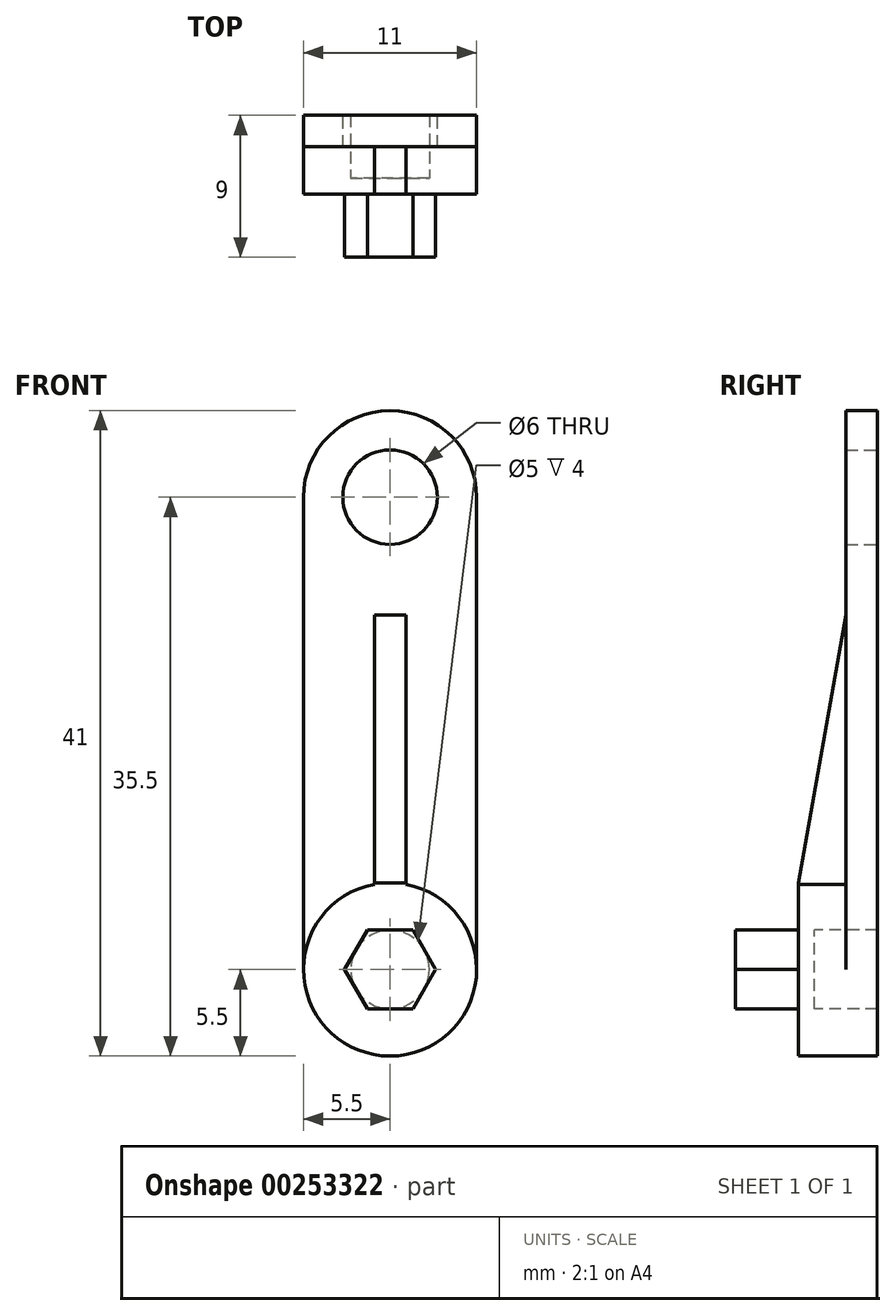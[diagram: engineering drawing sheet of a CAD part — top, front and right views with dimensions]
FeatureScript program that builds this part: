
annotation { "Feature Type Name" : "Feature", "Feature Type Description" : "" }
export const myFeature = defineFeature(function(context is Context, id is Id, definition is map)
    precondition{}
    {
        {
            var Q0;
            Q0=qCreatedBy(makeId("Front.planeOp"),FACE);
            var sketch = newSketch(context, id + "F0", { "sketchPlane" : qUnion([Q0])});
            skLineSegment(sketch, "E0", {"start": v(-5.5, 30) * mm, "end": v(-5.5, 0) * mm});
            skLineSegment(sketch, "E1", {"start": v(5.5, 30) * mm, "end": v(5.5, 0) * mm});
            skArc(sketch, "E2", {"start": v(5.5, 30) * mm, "mid": v(0, 35.5) * mm, "end": v(-5.5, 30) * mm});
            skCircle(sketch, "E3", {"center": v(0, 30) * mm, "radius": 3 * mm});
            skCircle(sketch, "E4", {"center": v(0, 0) * mm, "radius": 5.5 * mm});
            skCircle(sketch, "E5.cCircle", {"center": v(0, 0) * mm, "radius": 2.5 * mm, "construction": true});
            skLineSegment(sketch, "E5.0", {"start": v(-1.44, 2.5) * mm, "end": v(1.44, 2.5) * mm});
            skLineSegment(sketch, "E5.1", {"start": v(1.44, 2.5) * mm, "end": v(2.89, 0) * mm});
            skLineSegment(sketch, "E5.2", {"start": v(2.89, 0) * mm, "end": v(1.44, -2.5) * mm});
            skLineSegment(sketch, "E5.3", {"start": v(1.44, -2.5) * mm, "end": v(-1.44, -2.5) * mm});
            skLineSegment(sketch, "E5.4", {"start": v(-1.44, -2.5) * mm, "end": v(-2.89, 0) * mm});
            skLineSegment(sketch, "E5.5", {"start": v(-2.89, 0) * mm, "end": v(-1.44, 2.5) * mm});
            skPoint(sketch, "E5.0.midPoint", {"position": v(0, 2.5) * mm});
            skLineSegment(sketch, "E6", {"start": v(-5.5, 3.5) * mm, "end": v(4.64, -2.96) * mm, "construction": true});
            skSolve(sketch);
        }
        {
            var Q0;
            {var subQ1=sQuery(id+"F0.wireOp",EDGE,"E0");Q0=makeQuery(id+"F0.imprint","IMPRINT",FACE,{"disambiguationData":[TD([[makeQuery(id+"F0.imprint","IMPRINT",EDGE,{"derivedFrom":subQ1}),1.0]])]});}
            extrude(context, id + "F1", {"entities" : qUnion([Q0]), "depth" : 2 * mm});
        }
        {
            var Q0;
            Q0=makeQuery(id+"F0.imprint","IMPRINT",FACE,{"disambiguationData":[TD([[makeQuery(id+"F0.imprint","IMPRINT",EDGE,{"derivedFrom":sQuery(id+"F0.wireOp",EDGE,"E5.0")}),1.0]])]});
            extrude(context, id + "F2", {"entities" : qUnion([Q0]), "operationType" : NewBodyOperationType.ADD, "depth" : 5 * mm});
        }
        {
            var Q0;
            Q0=makeQuery(id+"F0.imprint","IMPRINT",FACE,{"disambiguationData":[TD([[makeQuery(id+"F0.imprint","IMPRINT",EDGE,{"derivedFrom":sQuery(id+"F0.wireOp",EDGE,"E5.0")}),-1.0]])]});
            extrude(context, id + "F3", {"entities" : qUnion([Q0]), "operationType" : NewBodyOperationType.ADD, "depth" : 9 * mm});
        }
        {
            var Q0;
            Q0=qCreatedBy(makeId("Right.planeOp"),FACE);
            var sketch = newSketch(context, id + "F4", { "sketchPlane" : qUnion([Q0])});
            skLineSegment(sketch, "E7.0", {"start": v(-5, -5.5) * mm, "end": v(-5, 5.5) * mm});
            skLineSegment(sketch, "E8.0", {"start": v(-2, 22.51) * mm, "end": v(-2, 5.5) * mm});
            skLineSegment(sketch, "E9", {"start": v(-5, 5.5) * mm, "end": v(-2, 22.51) * mm});
            skPoint(sketch, "E10.orphan", {"position": v(-2, 0) * mm});
            skPoint(sketch, "E11.orphan", {"position": v(-2, 30) * mm});
            skLineSegment(sketch, "E12.0", {"start": v(-2, 30) * mm, "end": v(-2, 0) * mm});
            skLineSegment(sketch, "E13", {"start": v(-2, 3.5) * mm, "end": v(-5, 3.5) * mm});
            skSolve(sketch);
        }
        {
            var Q0;
            Q0 = qSketchRegion(id + "F4", true);
            extrude(context, id + "F5", {"entities" : qUnion([Q0]), "operationType" : NewBodyOperationType.ADD, "endBound" : BoundingType.SYMMETRIC, "depth" : 2 * mm});
        }
        {
            var Q0;
            Q0=qCreatedBy(makeId("Right.planeOp"),FACE);
            var sketch = newSketch(context, id + "F6", { "sketchPlane" : qUnion([Q0])});
            skLineSegment(sketch, "E14.bottom", {"start": v(-4, 2.5) * mm, "end": v(0, 2.5) * mm});
            skLineSegment(sketch, "E14.top", {"start": v(-4, -2.5) * mm, "end": v(0, -2.5) * mm, "construction": true});
            skLineSegment(sketch, "E14.left", {"start": v(-4, 2.5) * mm, "end": v(-4, -2.5) * mm});
            skLineSegment(sketch, "E14.right", {"start": v(0, 2.5) * mm, "end": v(0, -2.5) * mm});
            skPoint(sketch, "E14.middle", {"position": v(-2, 0) * mm});
            skLineSegment(sketch, "E15", {"start": v(0, 0) * mm, "end": v(-4, 0) * mm});
            skSolve(sketch);
        }
        {
            var Q0;
            Q0 = qSketchRegion(id + "F6", true);
            var Q1;
            Q1=sQuery(id+"F6.wireOp",EDGE,"E15");
            revolve(context, id + "F7", {"operationType" : NewBodyOperationType.REMOVE, "entities" : qUnion([Q0]), "axis" : qUnion([Q1]), "revolveType" : RevolveType.FULL, "oppositeDirection" : true});
        }
    });
